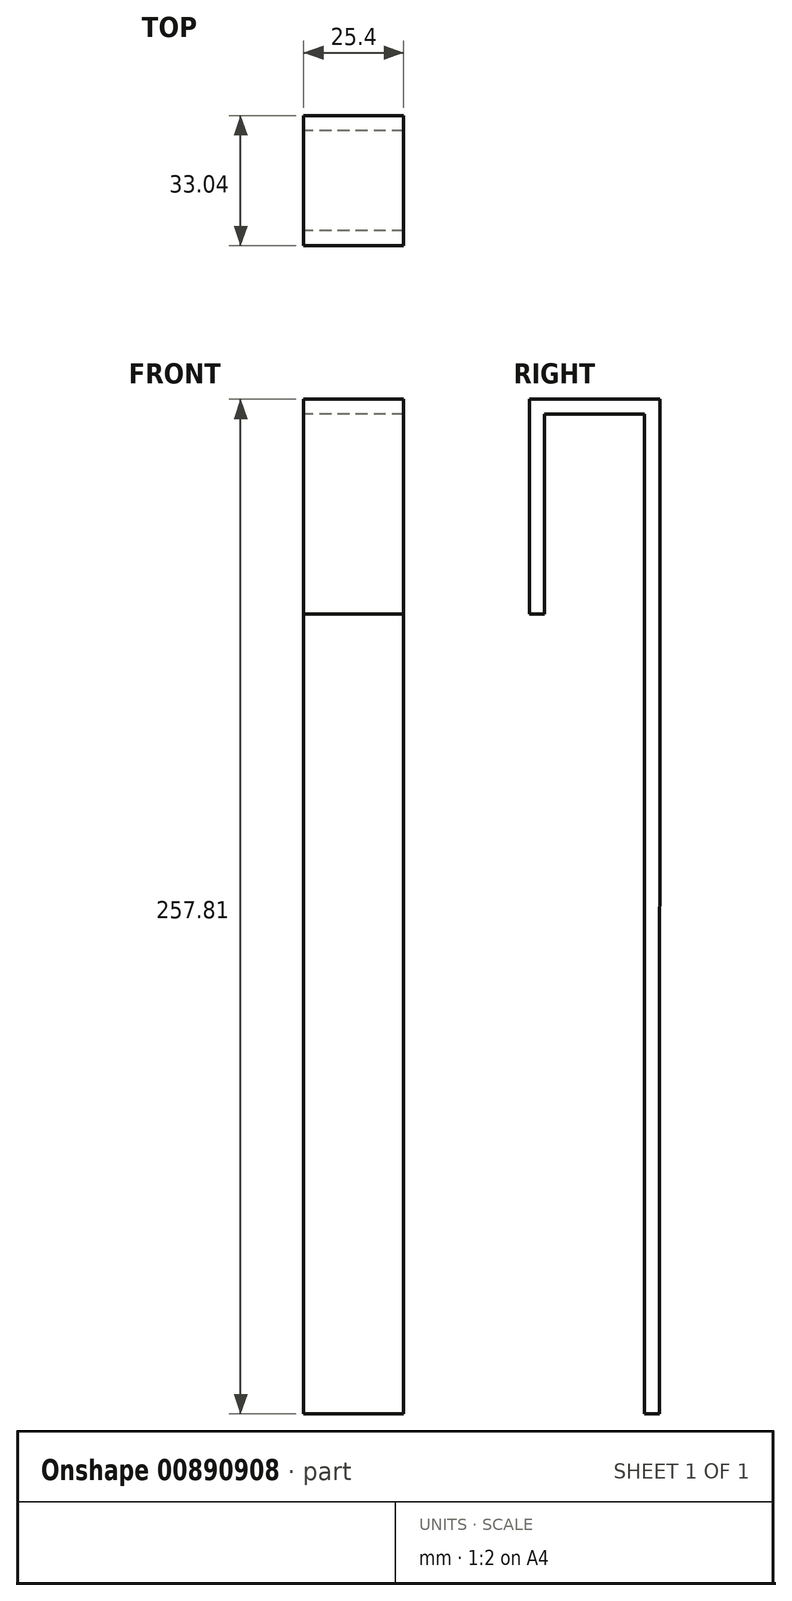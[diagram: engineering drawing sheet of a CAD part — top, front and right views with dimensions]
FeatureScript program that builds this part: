
annotation { "Feature Type Name" : "Feature", "Feature Type Description" : "" }
export const myFeature = defineFeature(function(context is Context, id is Id, definition is map)
    precondition{}
    {
        {
            var Q0;
            Q0=qCreatedBy(makeId("Right.planeOp"),FACE);
            var sketch = newSketch(context, id + "F0", { "sketchPlane" : qUnion([Q0])});
            skLineSegment(sketch, "E0", {"start": v(-40.18, 81.4) * mm, "end": v(-40.18, 30.6) * mm});
            skLineSegment(sketch, "E1", {"start": v(-40.18, 81.4) * mm, "end": v(-14.78, 81.4) * mm});
            skLineSegment(sketch, "E2", {"start": v(-14.78, 81.4) * mm, "end": v(-14.78, -172.6) * mm});
            skLineSegment(sketch, "E3", {"start": v(-14.78, -172.6) * mm, "end": v(-10.97, -172.6) * mm});
            skLineSegment(sketch, "E4", {"start": v(-10.94, 85.22) * mm, "end": v(-10.97, -172.6) * mm});
            skLineSegment(sketch, "E5", {"start": v(-10.94, 85.22) * mm, "end": v(-43.98, 85.22) * mm});
            skLineSegment(sketch, "E6", {"start": v(-40.18, 30.6) * mm, "end": v(-43.97, 30.6) * mm});
            skLineSegment(sketch, "E7", {"start": v(-43.98, 85.22) * mm, "end": v(-43.97, 30.6) * mm});
            skSolve(sketch);
        }
        {
            var Q0;
            Q0 = qSketchRegion(id + "F0", true);
            extrude(context, id + "F1", {"entities" : qUnion([Q0]), "depth" : 25.4 * mm, "offsetDistance" : 25.4 * mm});
        }
    });
